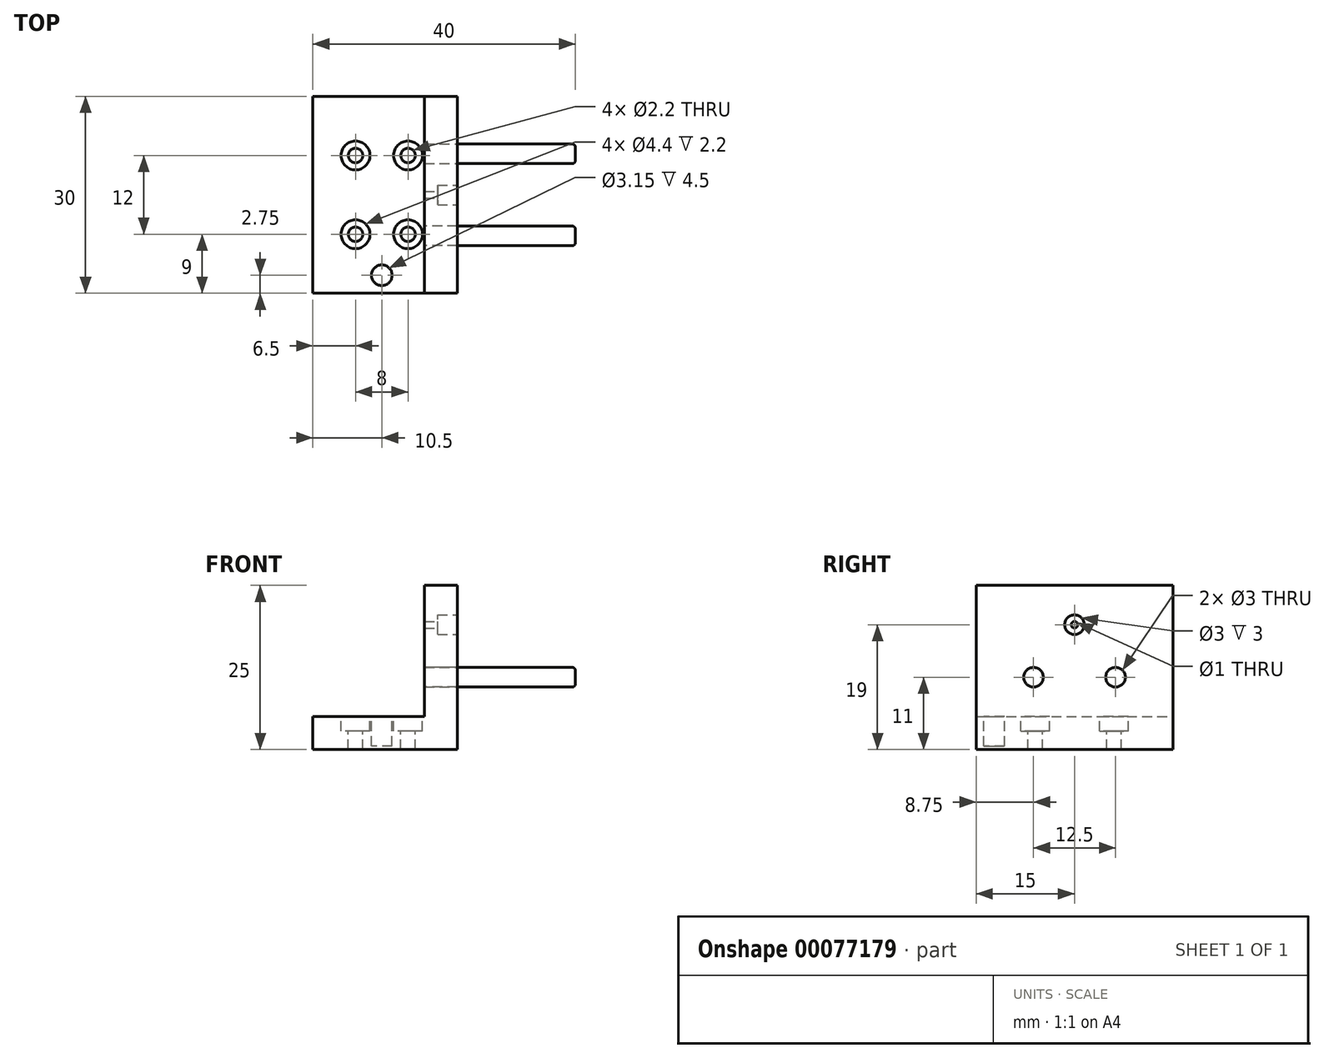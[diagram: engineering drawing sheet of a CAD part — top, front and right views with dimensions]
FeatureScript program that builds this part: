
annotation { "Feature Type Name" : "Feature", "Feature Type Description" : "" }
export const myFeature = defineFeature(function(context is Context, id is Id, definition is map)
    precondition{}
    {
        {
            var Q0;
            Q0=qCreatedBy(makeId("Top.planeOp"),FACE);
            var sketch = newSketch(context, id + "F0", { "sketchPlane" : qUnion([Q0])});
            skLineSegment(sketch, "E0.bottom", {"start": v(0, 0) * mm, "end": v(22, 0) * mm});
            skLineSegment(sketch, "E0.top", {"start": v(0, 30) * mm, "end": v(22, 30) * mm});
            skLineSegment(sketch, "E0.left", {"start": v(0, 0) * mm, "end": v(0, 30) * mm});
            skLineSegment(sketch, "E0.right", {"start": v(22, 0) * mm, "end": v(22, 30) * mm});
            skSolve(sketch);
        }
        {
            var Q0;
            Q0=qSketchRegion(id+"F0",true);
            extrude(context, id + "F1", {"entities" : qUnion([Q0]), "depth" : 5 * mm});
        }
        {
            var Q0;
            Q0=makeQuery(id+"F1.opExtrude","CAP_FACE",FACE,{"disambiguationData":[OSD([sQuery(id+"F0.wireOp",EDGE,"E0.bottom"),sQuery(id+"F0.wireOp",EDGE,"E0.top"),sQuery(id+"F0.wireOp",EDGE,"E0.left"),sQuery(id+"F0.wireOp",EDGE,"E0.right")])],"isStart":false});
            var sketch = newSketch(context, id + "F2", { "sketchPlane" : qUnion([Q0])});
            skLineSegment(sketch, "E1.bottom", {"start": v(22, 0) * mm, "end": v(17, 0) * mm});
            skLineSegment(sketch, "E1.top", {"start": v(22, 30) * mm, "end": v(17, 30) * mm});
            skLineSegment(sketch, "E1.left", {"start": v(22, 0) * mm, "end": v(22, 30) * mm});
            skLineSegment(sketch, "E1.right", {"start": v(17, 0) * mm, "end": v(17, 30) * mm});
            skSolve(sketch);
        }
        {
            var Q0;
            Q0=qSketchRegion(id+"F2",true);
            extrude(context, id + "F3", {"entities" : qUnion([Q0]), "operationType" : NewBodyOperationType.ADD, "depth" : 20 * mm});
        }
        {
            var Q0;
            Q0=makeQuery(id+"F1.opExtrude","CAP_FACE",FACE,{"disambiguationData":[OSD([sQuery(id+"F0.wireOp",EDGE,"E0.bottom"),sQuery(id+"F0.wireOp",EDGE,"E0.top"),sQuery(id+"F0.wireOp",EDGE,"E0.left"),sQuery(id+"F0.wireOp",EDGE,"E0.right")])],"isStart":false});
            var sketch = newSketch(context, id + "F4", { "sketchPlane" : qUnion([Q0])});
            skPoint(sketch, "E2", {"position": v(6.5, 21) * mm});
            skPoint(sketch, "E3", {"position": v(14.5, 21) * mm});
            skPoint(sketch, "E4", {"position": v(6.5, 9) * mm});
            skPoint(sketch, "E5", {"position": v(14.5, 9) * mm});
            skSolve(sketch);
        }
        {
            var Q0;
            Q0=sQuery(id+"F4.wireOp",VERTEX,"E4");
            var Q1;
            Q1=sQuery(id+"F4.wireOp",VERTEX,"E2");
            var Q2;
            Q2=sQuery(id+"F4.wireOp",VERTEX,"E3");
            var Q3;
            Q3=sQuery(id+"F4.wireOp",VERTEX,"E5");
            var Q4;
            Q4=makeQuery(id+"F1.opExtrude","SWEPT_BODY",BODY,{"disambiguationData":[OSD([sQuery(id+"F0.wireOp",EDGE,"E0.bottom"),sQuery(id+"F0.wireOp",EDGE,"E0.top"),sQuery(id+"F0.wireOp",EDGE,"E0.left"),sQuery(id+"F0.wireOp",EDGE,"E0.right")])]});
            hole(context, id + "F5", {"style" : HoleStyle.C_BORE, "holeDiameter" : 2.2 * mm, "cBoreDiameter" : 4.4 * mm, "cBoreDepth" : 2.2 * mm, "endStyle" : HoleEndStyle.THROUGH, "locations" : qUnion([Q0, Q1, Q2, Q3]), "scope" : qUnion([Q4])});
        }
        {
            var Q0;
            Q0=makeQuery(id+"F3.boolean.opBoolean","MERGE",FACE,{"derivedFrom":[makeQuery(id+"F1.opExtrude","SWEPT_FACE",FACE,{"disambiguationData":[OSD([sQuery(id+"F0.wireOp",EDGE,"E0.right")])]}),makeQuery(id+"F3.opExtrude","SWEPT_FACE",FACE,{"disambiguationData":[OSD([sQuery(id+"F2.wireOp",EDGE,"E1.left")])]})]});
            var sketch = newSketch(context, id + "F6", { "sketchPlane" : qUnion([Q0])});
            skCircle(sketch, "E6", {"center": v(8.75, 11) * mm, "radius": 1.5 * mm});
            skCircle(sketch, "E7", {"center": v(21.25, 11) * mm, "radius": 1.5 * mm});
            skSolve(sketch);
        }
        {
            var Q0;
            Q0=qSketchRegion(id+"F6",true);
            extrude(context, id + "F7", {"entities" : qUnion([Q0]), "operationType" : NewBodyOperationType.REMOVE, "oppositeDirection" : true, "depth" : 25 * mm});
        }
        {
            var Q0;
            Q0=makeQuery(id+"F3.opExtrude","SWEPT_FACE",FACE,{"disambiguationData":[OSD([sQuery(id+"F2.wireOp",EDGE,"E1.right")])]});
            var sketch = newSketch(context, id + "F8", { "sketchPlane" : qUnion([Q0])});
            skCircle(sketch, "E8", {"center": v(-8.75, 11) * mm, "radius": 1.5 * mm});
            skCircle(sketch, "E9", {"center": v(-21.25, 11) * mm, "radius": 1.5 * mm});
            skSolve(sketch);
        }
        {
            var Q0;
            Q0=qSketchRegion(id+"F8",true);
            extrude(context, id + "F9", {"entities" : qUnion([Q0]), "oppositeDirection" : true, "depth" : 23 * mm});
        }
        {
            var Q0;
            Q0=makeQuery(id+"F9.opExtrude","CAP_EDGE",EDGE,{"disambiguationData":[OSD([sQuery(id+"F8.wireOp",EDGE,"E8")])],"isStart":false});
            var Q1;
            Q1=makeQuery(id+"F9.opExtrude","CAP_EDGE",EDGE,{"disambiguationData":[OSD([sQuery(id+"F8.wireOp",EDGE,"E9")])],"isStart":false});
            fillet(context, id + "F10", {"entities" : qUnion([Q0, Q1]), "radius" : .5 * mm, "tangentPropagation" : true, "allowEdgeOverflow" : false});
        }
        {
            var Q0;
            Q0=makeQuery(id+"F1.opExtrude","CAP_FACE",FACE,{"disambiguationData":[OSD([sQuery(id+"F0.wireOp",EDGE,"E0.bottom"),sQuery(id+"F0.wireOp",EDGE,"E0.top"),sQuery(id+"F0.wireOp",EDGE,"E0.left"),sQuery(id+"F0.wireOp",EDGE,"E0.right")])],"isStart":false});
            var sketch = newSketch(context, id + "F11", { "sketchPlane" : qUnion([Q0])});
            skCircle(sketch, "E10", {"center": v(10.5, 2.75) * mm, "radius": 1.57 * mm});
            skSolve(sketch);
        }
        {
            var Q0;
            Q0=qSketchRegion(id+"F11",true);
            extrude(context, id + "F12", {"entities" : qUnion([Q0]), "operationType" : NewBodyOperationType.REMOVE, "oppositeDirection" : true, "depth" : 4.5 * mm});
        }
        {
            var Q0;
            Q0=makeQuery(id+"F3.boolean.opBoolean","MERGE",FACE,{"derivedFrom":[makeQuery(id+"F1.opExtrude","SWEPT_FACE",FACE,{"disambiguationData":[OSD([sQuery(id+"F0.wireOp",EDGE,"E0.right")])]}),makeQuery(id+"F3.opExtrude","SWEPT_FACE",FACE,{"disambiguationData":[OSD([sQuery(id+"F2.wireOp",EDGE,"E1.left")])]})]});
            var sketch = newSketch(context, id + "F13", { "sketchPlane" : qUnion([Q0])});
            skCircle(sketch, "E11", {"center": v(15, 19) * mm, "radius": 1.5 * mm});
            skSolve(sketch);
        }
        {
            var Q0;
            Q0=qSketchRegion(id+"F13",true);
            extrude(context, id + "F14", {"entities" : qUnion([Q0]), "operationType" : NewBodyOperationType.REMOVE, "oppositeDirection" : true, "depth" : 3 * mm});
        }
        {
            var Q0;
            Q0=makeQuery(id+"F14.boolean.opBoolean","COPY",FACE,{"derivedFrom":makeQuery(id+"F14.opExtrude","CAP_FACE",FACE,{"disambiguationData":[OSD([sQuery(id+"F13.wireOp",EDGE,"E11")])],"isStart":false})});
            var sketch = newSketch(context, id + "F15", { "sketchPlane" : qUnion([Q0])});
            skCircle(sketch, "E12", {"center": v(15, 19) * mm, "radius": 0.5 * mm});
            skSolve(sketch);
        }
        {
            var Q0;
            Q0=qSketchRegion(id+"F15",true);
            extrude(context, id + "F16", {"entities" : qUnion([Q0]), "operationType" : NewBodyOperationType.REMOVE, "oppositeDirection" : true, "depth" : 25 * mm});
        }
    });
